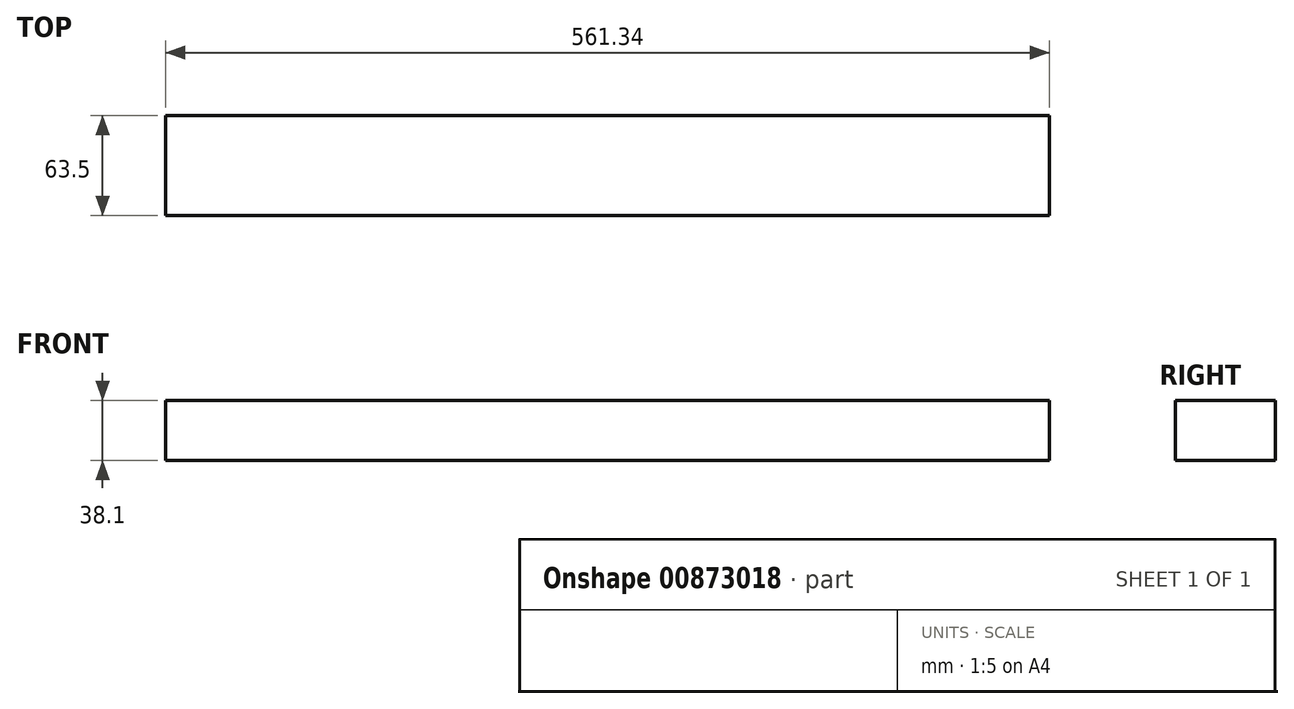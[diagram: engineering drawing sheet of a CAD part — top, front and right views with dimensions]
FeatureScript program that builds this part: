
annotation { "Feature Type Name" : "Feature", "Feature Type Description" : "" }
export const myFeature = defineFeature(function(context is Context, id is Id, definition is map)
    precondition{}
    {
        {
            var Q0;
            Q0=qCreatedBy(makeId("Top.planeOp"),FACE);
            var sketch = newSketch(context, id + "F0", { "sketchPlane" : qUnion([Q0])});
            skLineSegment(sketch, "E0.bottom", {"start": v(-53.97, -21.26) * mm, "end": v(507.37, -21.26) * mm});
            skLineSegment(sketch, "E0.top", {"start": v(-53.97, 42.24) * mm, "end": v(507.37, 42.24) * mm});
            skLineSegment(sketch, "E0.left", {"start": v(-53.97, -21.26) * mm, "end": v(-53.97, 42.24) * mm});
            skLineSegment(sketch, "E0.right", {"start": v(507.37, -21.26) * mm, "end": v(507.37, 42.24) * mm});
            skSolve(sketch);
        }
        {
            var Q0;
            Q0=makeQuery(id+"F0.imprint","IMPRINT",FACE,{"disambiguationData":[TD([[makeQuery(id+"F0.imprint","IMPRINT",EDGE,{"derivedFrom":sQuery(id+"F0.wireOp",EDGE,"E0.bottom")}),1.0]])]});
            extrude(context, id + "F1", {"entities" : qUnion([Q0]), "depth" : 38.1 * mm, "offsetDistance" : 25.4 * mm});
        }
    });
